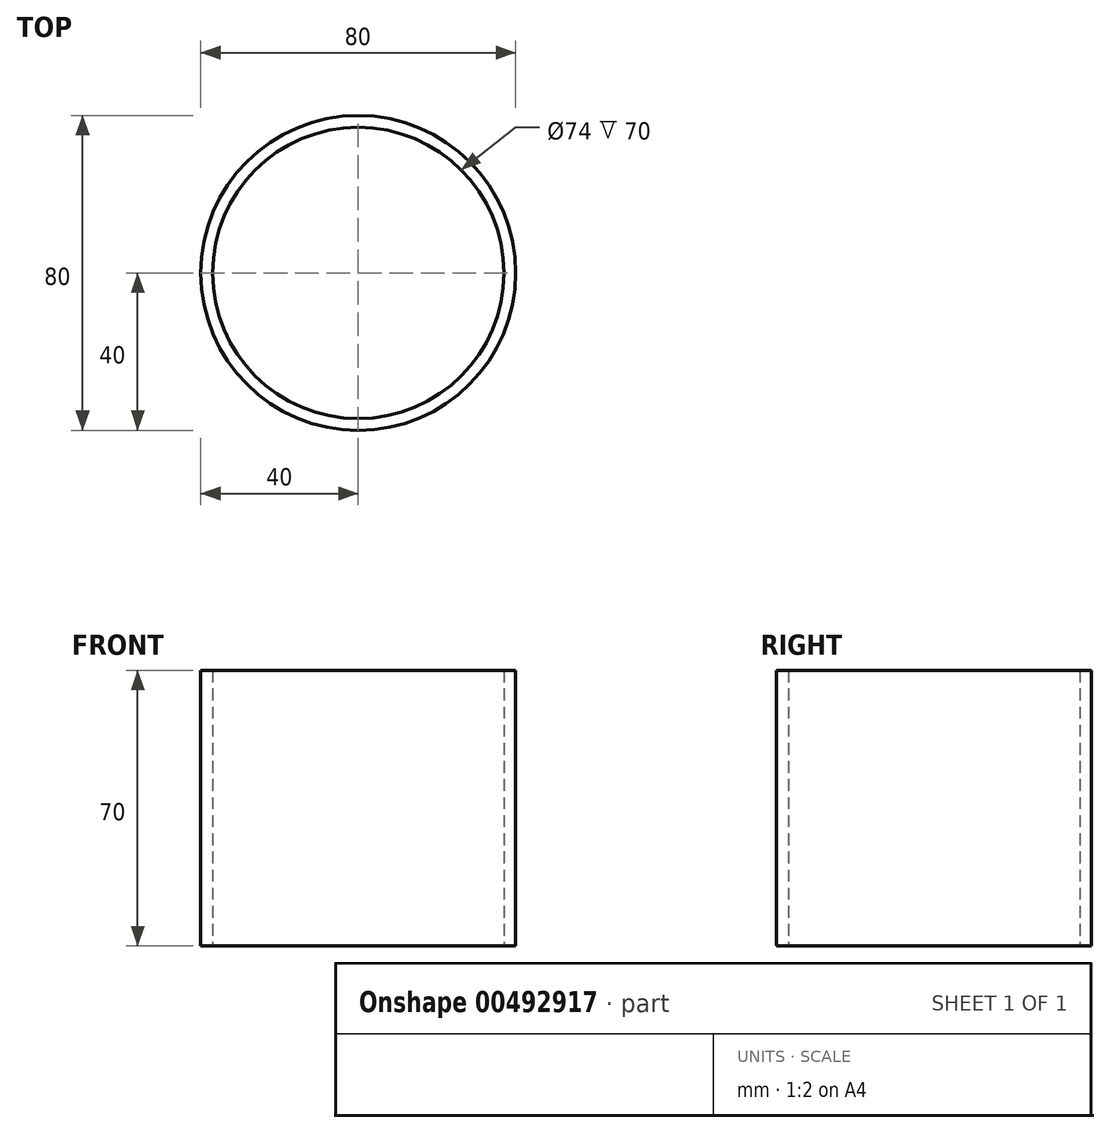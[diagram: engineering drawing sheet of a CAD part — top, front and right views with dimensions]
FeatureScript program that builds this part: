
annotation { "Feature Type Name" : "Feature", "Feature Type Description" : "" }
export const myFeature = defineFeature(function(context is Context, id is Id, definition is map)
    precondition{}
    {
        {
            var Q0;
            Q0=qCreatedBy(makeId("Top.planeOp"),FACE);
            var sketch = newSketch(context, id + "F0", { "sketchPlane" : qUnion([Q0])});
            skCircle(sketch, "E0", {"center": v(0, 0) * mm, "radius": 40 * mm});
            skCircle(sketch, "E1", {"center": v(0, 0) * mm, "radius": 37 * mm});
            skSolve(sketch);
        }
        {
            var Q0;
            Q0=makeQuery(id+"F0.imprint","IMPRINT",FACE,{"disambiguationData":[TD([[makeQuery(id+"F0.imprint","IMPRINT",EDGE,{"derivedFrom":sQuery(id+"F0.wireOp",EDGE,"E0")}),1.0]])]});
            extrude(context, id + "F1", {"entities" : qUnion([Q0]), "depth" : 70 * mm});
        }
    });
